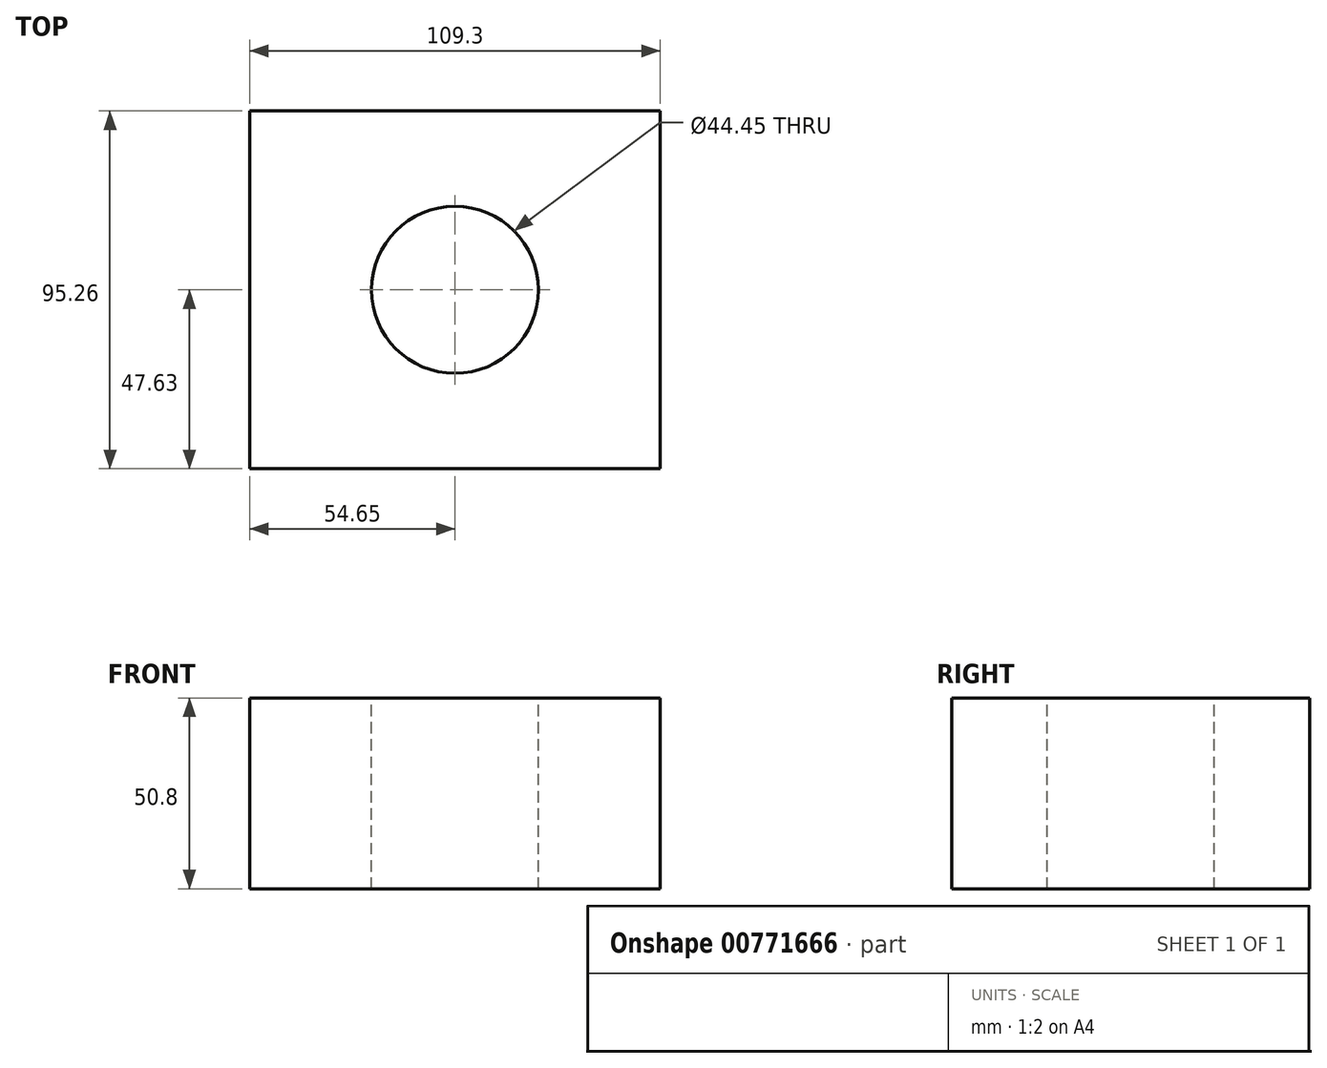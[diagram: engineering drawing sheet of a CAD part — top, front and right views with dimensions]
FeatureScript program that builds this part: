
annotation { "Feature Type Name" : "Feature", "Feature Type Description" : "" }
export const myFeature = defineFeature(function(context is Context, id is Id, definition is map)
    precondition{}
    {
        {
            var Q0;
            Q0=qCreatedBy(makeId("Top.planeOp"),FACE);
            var sketch = newSketch(context, id + "F0", { "sketchPlane" : qUnion([Q0])});
            skLineSegment(sketch, "E0.bottom", {"start": v(54.65, 47.63) * mm, "end": v(-54.65, 47.63) * mm});
            skLineSegment(sketch, "E0.top", {"start": v(54.65, -47.63) * mm, "end": v(-54.65, -47.63) * mm});
            skLineSegment(sketch, "E0.left", {"start": v(54.65, 47.63) * mm, "end": v(54.65, -47.63) * mm});
            skLineSegment(sketch, "E0.right", {"start": v(-54.65, 47.63) * mm, "end": v(-54.65, -47.63) * mm});
            skPoint(sketch, "E0.middle", {"position": v(0, 0) * mm});
            skSolve(sketch);
        }
        {
            var Q0;
            Q0 = qSketchRegion(id + "F0", true);
            var Q1;
            Q1=makeQuery(id+"F0.imprint","IMPRINT",FACE,{"disambiguationData":[TD([[makeQuery(id+"F0.imprint","IMPRINT",EDGE,{"derivedFrom":sQuery(id+"F0.wireOp",EDGE,"E0.bottom")}),1.0]])]});
            extrude(context, id + "F1", {"entities" : qUnion([Q0, Q1]), "depth" : 50.8 * mm, "offsetDistance" : 25.4 * mm});
        }
        {
            var Q0;
            Q0=makeQuery(id+"F1.opExtrude","CAP_FACE",FACE,{"disambiguationData":[OSD([sQuery(id+"F0.wireOp",EDGE,"E0.bottom"),sQuery(id+"F0.wireOp",EDGE,"E0.top"),sQuery(id+"F0.wireOp",EDGE,"E0.left"),sQuery(id+"F0.wireOp",EDGE,"E0.right")])],"isStart":false});
            var sketch = newSketch(context, id + "F2", { "sketchPlane" : qUnion([Q0])});
            skPoint(sketch, "E1", {"position": v(0, 0) * mm});
            skSolve(sketch);
        }
        {
            var Q0;
            Q0=sQuery(id+"F2.wireOp",VERTEX,"E1");
            var Q1;
            Q1=makeQuery(id+"F1.opExtrude","SWEPT_BODY",BODY,{"disambiguationData":[OSD([sQuery(id+"F0.wireOp",EDGE,"E0.bottom"),sQuery(id+"F0.wireOp",EDGE,"E0.top"),sQuery(id+"F0.wireOp",EDGE,"E0.left"),sQuery(id+"F0.wireOp",EDGE,"E0.right")])]});
            hole(context, id + "F3", {"style" : HoleStyle.SIMPLE, "endStyle" : HoleEndStyle.THROUGH, "standardTappedOrClearance" : lookupTablePath({ "fit" : "Normal", "standard" : "Custom", "size" : "1/4", "type" : "Clearance" }), "standardBlindInLast" : lookupTablePath({ "fit" : "Free", "standard" : "Custom", "size" : "1/4", "type" : "Clearance" }), "holeDiameter" : 44.45 * mm, "majorDiameter" : 6.35 * mm, "isTappedThrough" : true, "tappedDepth" : 12.7 * mm, "tapClearance" : 3, "locations" : qUnion([Q0]), "scope" : qUnion([Q1])});
        }
    });
